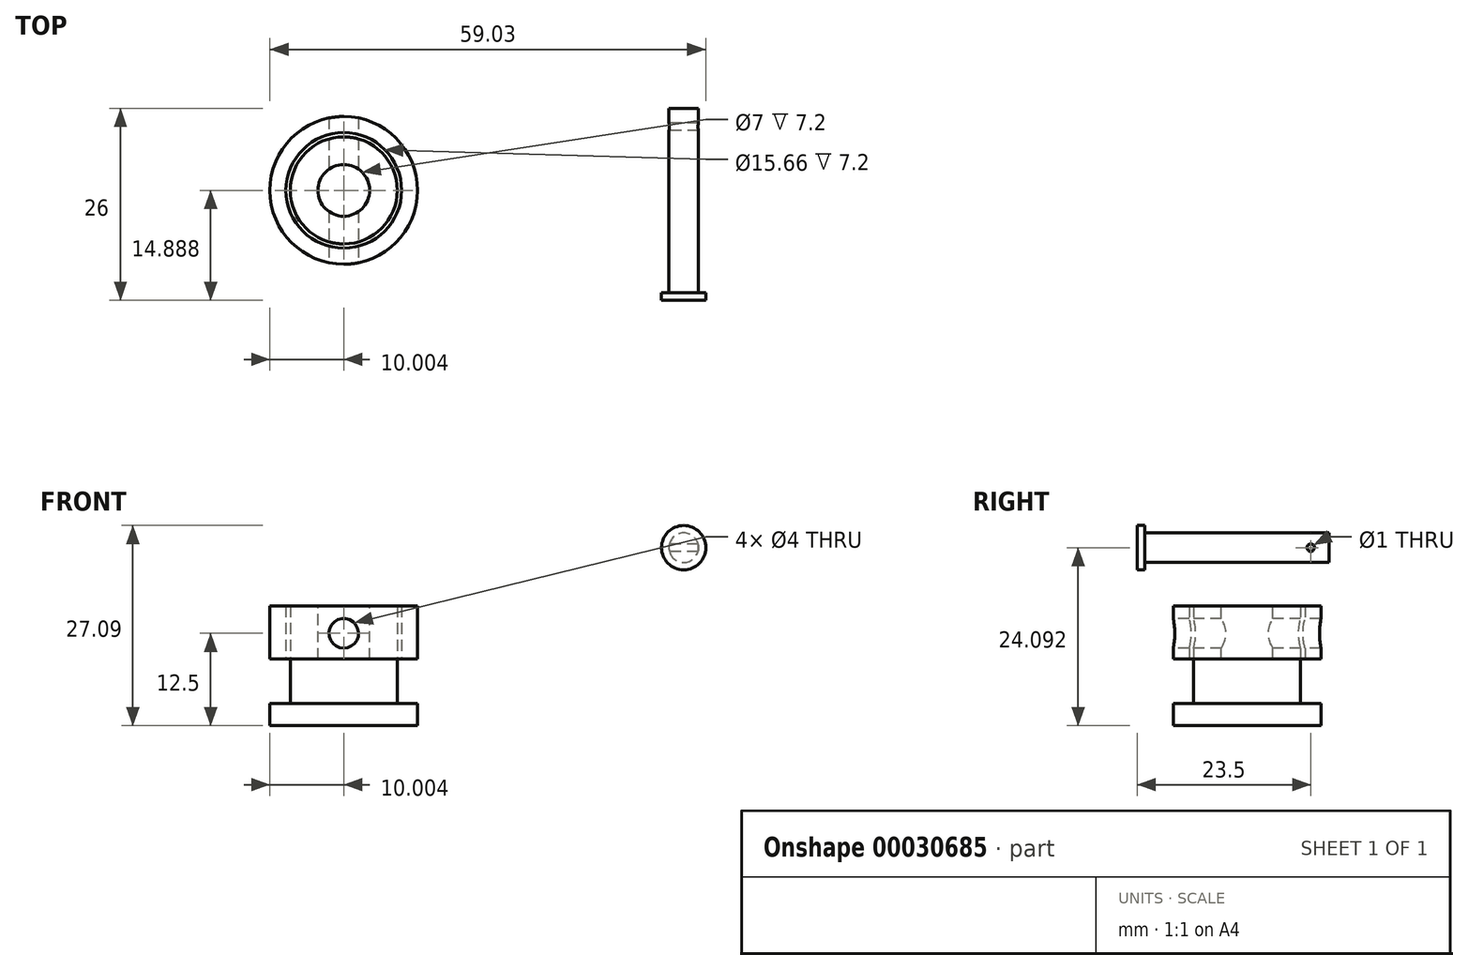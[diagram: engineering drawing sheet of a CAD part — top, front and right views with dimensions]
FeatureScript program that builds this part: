
annotation { "Feature Type Name" : "Feature", "Feature Type Description" : "" }
export const myFeature = defineFeature(function(context is Context, id is Id, definition is map)
    precondition{}
    {
        {
            var Q0;
            Q0=qCreatedBy(makeId("Top.planeOp"),FACE);
            var sketch = newSketch(context, id + "F0", { "sketchPlane" : qUnion([Q0])});
            skCircle(sketch, "E0", {"center": v(-31.7, 83.89) * mm, "radius": 10 * mm});
            skCircle(sketch, "E1", {"center": v(-31.7, 83.89) * mm, "radius": 7.83 * mm});
            skSolve(sketch);
        }
        {
            var Q0;
            Q0=qSketchRegion(id+"F0",true);
            var Q1;
            Q1=makeQuery(id+"F0.imprint","IMPRINT",FACE,{"disambiguationData":[TD([[makeQuery(id+"F0.imprint","IMPRINT",EDGE,{"derivedFrom":sQuery(id+"F0.wireOp",EDGE,"E0")}),1.0]])]});
            extrude(context, id + "F1", {"entities" : qUnion([Q0, Q1]), "depth" : 7 * mm, "hasSecondDirection" : true, "secondDirectionOppositeDirection" : true, "secondDirectionDepth" : 0.2 * mm});
        }
        {
            var Q0;
            Q0=qCreatedBy(makeId("Front.planeOp"),FACE);
            var sketch = newSketch(context, id + "F2", { "sketchPlane" : qUnion([Q0])});
            skCircle(sketch, "E2", {"center": v(-31.7, 3.3) * mm, "radius": 2 * mm});
            skLineSegment(sketch, "E3.0", {"start": v(-41.7, 7) * mm, "end": v(-21.7, 7) * mm});
            skLineSegment(sketch, "E4", {"start": v(-41.7, 0) * mm, "end": v(-41.7, 7) * mm});
            skLineSegment(sketch, "E5", {"start": v(-21.7, 7) * mm, "end": v(-21.7, 0) * mm});
            skSolve(sketch);
        }
        {
            var Q0;
            Q0=makeQuery(id+"F1.opExtrude","CAP_FACE",FACE,{"disambiguationData":[OSD([sQuery(id+"F0.wireOp",EDGE,"E0"),sQuery(id+"F0.wireOp",EDGE,"E1")])],"isStart":true});
            var sketch = newSketch(context, id + "F3", { "sketchPlane" : qUnion([Q0])});
            skCircle(sketch, "E6.0", {"center": v(-31.7, -83.89) * mm, "radius": 7.83 * mm});
            skCircle(sketch, "E7.0", {"center": v(-31.7, -83.89) * mm, "radius": 10 * mm});
            skCircle(sketch, "E8.0", {"center": v(-31.7, -83.89) * mm, "radius": 7.25 * mm});
            skSolve(sketch);
        }
        {
            var Q0;
            Q0=makeQuery(id+"F3.imprint","IMPRINT",FACE,{"disambiguationData":[TD([[makeQuery(id+"F3.imprint","IMPRINT",EDGE,{"derivedFrom":sQuery(id+"F3.wireOp",EDGE,"E8.0")}),1.0]])]});
            var Q1;
            Q1=makeQuery(id+"F1.opExtrude","CAP_FACE",FACE,{"disambiguationData":[OSD([sQuery(id+"F0.wireOp",EDGE,"E0"),sQuery(id+"F0.wireOp",EDGE,"E1")])],"isStart":false});
            extrude(context, id + "F4", {"entities" : qUnion([Q0]), "endBound" : BoundingType.UP_TO_SURFACE, "oppositeDirection" : true, "endBoundEntityFace" : qUnion([Q1]), "depth" : 25 * mm, "hasSecondDirection" : true, "secondDirectionOppositeDirection" : false, "secondDirectionDepth" : 6 * mm});
        }
        {
            var Q0;
            Q0=makeQuery(id+"F3.imprint","IMPRINT",FACE,{"disambiguationData":[TD([[makeQuery(id+"F3.imprint","IMPRINT",EDGE,{"derivedFrom":sQuery(id+"F3.wireOp",EDGE,"E8.0")}),1.0]])]});
            var Q1;
            Q1=makeQuery(id+"F3.imprint","IMPRINT",FACE,{"disambiguationData":[TD([[makeQuery(id+"F3.imprint","IMPRINT",EDGE,{"derivedFrom":sQuery(id+"F3.wireOp",EDGE,"E6.0")}),-1.0]])]});
            var Q2;
            Q2=makeQuery(id+"F3.imprint","IMPRINT",FACE,{"disambiguationData":[TD([[makeQuery(id+"F3.imprint","IMPRINT",EDGE,{"derivedFrom":sQuery(id+"F3.wireOp",EDGE,"E6.0")}),1.0]])]});
            extrude(context, id + "F5", {"entities" : qUnion([Q0, Q1, Q2]), "operationType" : NewBodyOperationType.ADD, "depth" : 9 * mm, "hasSecondDirection" : true, "secondDirectionOppositeDirection" : false, "secondDirectionDepth" : 6 * mm});
        }
        {
            var Q0;
            Q0=qCreatedBy(makeId("Front.planeOp"),FACE);
            cPlane(context, id + "F6", {"entities" : qUnion([Q0]), "cplaneType" : CPlaneType.OFFSET, "offset" : 70 * mm, "oppositeDirection" : true, "width" : 150 * mm, "height" : 150 * mm});
        }
        {
            var Q0;
            Q0=qCreatedBy(id+"F6.planeOp",FACE);
            var sketch = newSketch(context, id + "F7", { "sketchPlane" : qUnion([Q0])});
            skCircle(sketch, "E9", {"center": v(14.33, 14.9) * mm, "radius": 2 * mm});
            skCircle(sketch, "E10", {"center": v(14.33, 14.9) * mm, "radius": 3 * mm});
            skSolve(sketch);
        }
        {
            var Q0;
            Q0=makeQuery(id+"F1.opExtrude","CAP_FACE",FACE,{"disambiguationData":[OSD([sQuery(id+"F0.wireOp",EDGE,"E0"),sQuery(id+"F0.wireOp",EDGE,"E1")])],"isStart":false});
            var sketch = newSketch(context, id + "F8", { "sketchPlane" : qUnion([Q0])});
            skCircle(sketch, "E11", {"center": v(-31.7, 83.89) * mm, "radius": 3.5 * mm});
            skSolve(sketch);
        }
        {
            var Q0;
            Q0=makeQuery(id+"F8.imprint","IMPRINT",FACE,{"disambiguationData":[TD([[makeQuery(id+"F8.imprint","IMPRINT",EDGE,{"derivedFrom":sQuery(id+"F8.wireOp",EDGE,"E11")}),1.0]])]});
            var Q1;
            Q1=makeQuery(id+"F1.opExtrude","CAP_FACE",FACE,{"disambiguationData":[OSD([sQuery(id+"F0.wireOp",EDGE,"E0"),sQuery(id+"F0.wireOp",EDGE,"E1")])],"isStart":true});
            extrude(context, id + "F9", {"entities" : qUnion([Q0]), "operationType" : NewBodyOperationType.REMOVE, "endBound" : BoundingType.UP_TO_SURFACE, "oppositeDirection" : true, "endBoundEntityFace" : qUnion([Q1]), "depth" : 3 * mm});
        }
        {
            var Q0;
            Q0=qSketchRegion(id+"F2",true);
            var Q1;
            Q1=makeQuery(id+"F2.imprint","IMPRINT",FACE,{"disambiguationData":[TD([[makeQuery(id+"F2.imprint","IMPRINT",EDGE,{"derivedFrom":sQuery(id+"F2.wireOp",EDGE,"E2")}),1.0]])]});
            extrude(context, id + "F10", {"entities" : qUnion([Q0, Q1]), "operationType" : NewBodyOperationType.REMOVE, "endBound" : BoundingType.THROUGH_ALL, "oppositeDirection" : true, "depth" : 25 * mm});
        }
        {
            var Q0;
            Q0=makeQuery(id+"F7.imprint","IMPRINT",FACE,{"disambiguationData":[TD([[makeQuery(id+"F7.imprint","IMPRINT",EDGE,{"derivedFrom":sQuery(id+"F7.wireOp",EDGE,"E9")}),1.0]])]});
            extrude(context, id + "F11", {"entities" : qUnion([Q0]), "oppositeDirection" : true, "depth" : 25 * mm});
        }
        {
            var Q0;
            Q0=makeQuery(id+"F7.imprint","IMPRINT",FACE,{"disambiguationData":[TD([[makeQuery(id+"F7.imprint","IMPRINT",EDGE,{"derivedFrom":sQuery(id+"F7.wireOp",EDGE,"E9")}),-1.0]])]});
            var Q1;
            Q1=makeQuery(id+"F7.imprint","IMPRINT",FACE,{"disambiguationData":[TD([[makeQuery(id+"F7.imprint","IMPRINT",EDGE,{"derivedFrom":sQuery(id+"F7.wireOp",EDGE,"E9")}),1.0]])]});
            extrude(context, id + "F12", {"entities" : qUnion([Q0, Q1]), "operationType" : NewBodyOperationType.ADD, "depth" : 1 * mm});
        }
        {
            var Q0;
            Q0=qCreatedBy(makeId("Right.planeOp"),FACE);
            var sketch = newSketch(context, id + "F13", { "sketchPlane" : qUnion([Q0])});
            skCircle(sketch, "E12", {"center": v(92.5, 14.9) * mm, "radius": 0.5 * mm});
            skLineSegment(sketch, "E13.0", {"start": v(95, 12.9) * mm, "end": v(95, 16.9) * mm});
            skSolve(sketch);
        }
        {
            var Q0;
            Q0=makeQuery(id+"F13.imprint","IMPRINT",FACE,{"disambiguationData":[TD([[makeQuery(id+"F13.imprint","IMPRINT",EDGE,{"derivedFrom":sQuery(id+"F13.wireOp",EDGE,"E12")}),1.0]])]});
            extrude(context, id + "F14", {"entities" : qUnion([Q0]), "operationType" : NewBodyOperationType.REMOVE, "depth" : 25 * mm});
        }
    });
